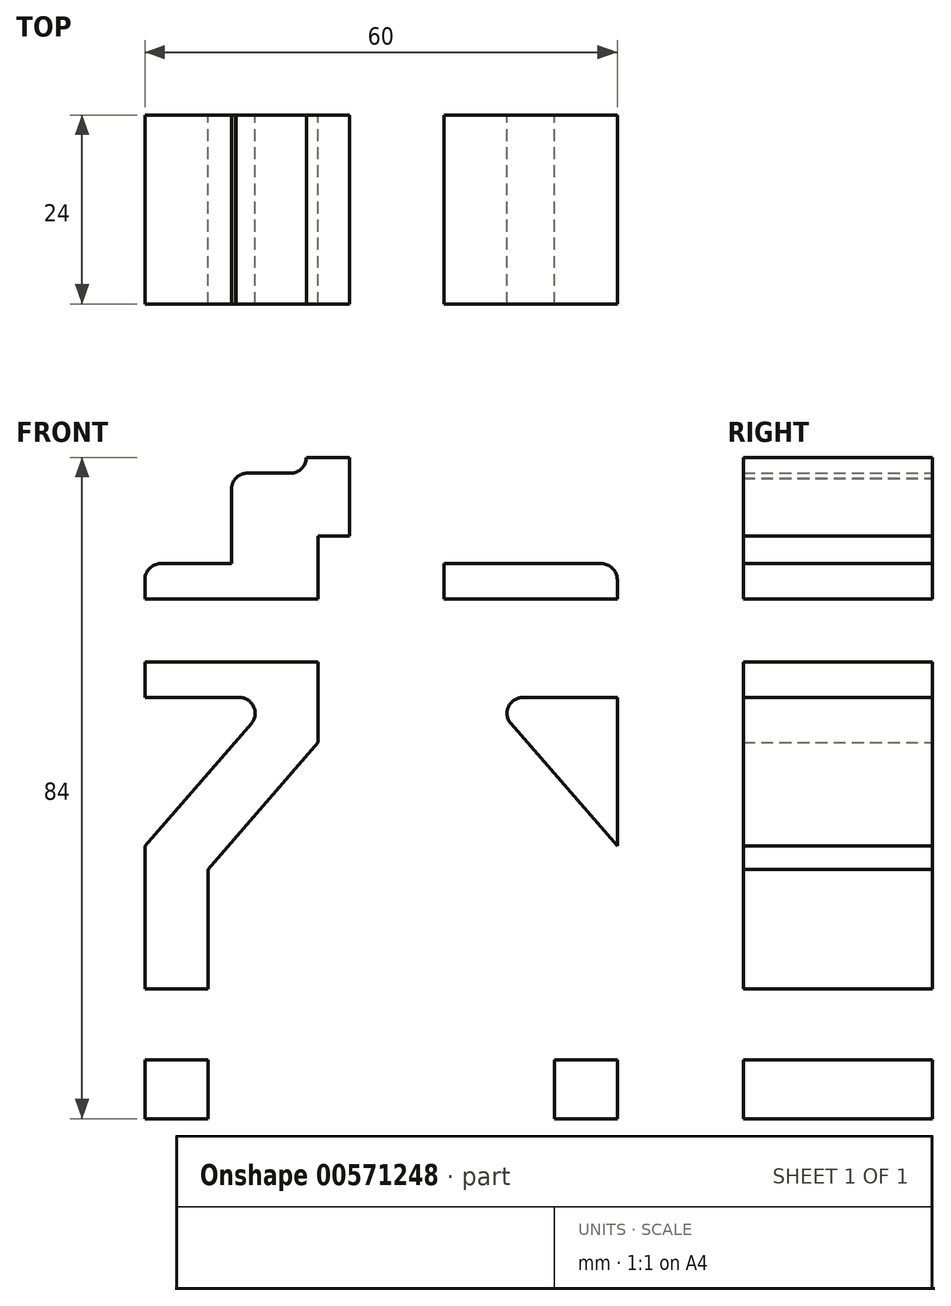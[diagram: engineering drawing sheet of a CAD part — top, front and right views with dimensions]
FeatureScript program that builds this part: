
annotation { "Feature Type Name" : "Feature", "Feature Type Description" : "" }
export const myFeature = defineFeature(function(context is Context, id is Id, definition is map)
    precondition{}
    {
        {
            var Q0;
            Q0=qCreatedBy(makeId("Front.planeOp"),FACE);
            var sketch = newSketch(context, id + "F0", { "sketchPlane" : qUnion([Q0])});
            skLineSegment(sketch, "E0", {"start": v(0, 0) * mm, "end": v(0, 72) * mm, "construction": true});
            skLineSegment(sketch, "E1", {"start": v(0, 72) * mm, "end": v(-4, 72) * mm});
            skLineSegment(sketch, "E2", {"start": v(-4, 72) * mm, "end": v(-4, 62) * mm});
            skLineSegment(sketch, "E3", {"start": v(0, 62) * mm, "end": v(-8, 62) * mm});
            skLineSegment(sketch, "E4", {"start": v(-8, 62) * mm, "end": v(-8, 35.76) * mm});
            skLineSegment(sketch, "E5", {"start": v(0, 50) * mm, "end": v(-30, 50) * mm, "construction": true});
            skLineSegment(sketch, "E6", {"start": v(-30, 54) * mm, "end": v(-8, 54) * mm});
            skLineSegment(sketch, "E7.MirrorCS", {"start": v(-30, 46) * mm, "end": v(-8, 46) * mm});
            skLineSegment(sketch, "E8", {"start": v(-22, 19.66) * mm, "end": v(-22, -12) * mm});
            skLineSegment(sketch, "E9", {"start": v(-22, -12) * mm, "end": v(-30, -12) * mm});
            skLineSegment(sketch, "E10", {"start": v(-30, 0) * mm, "end": v(0, 0) * mm, "construction": true});
            skLineSegment(sketch, "E11", {"start": v(-30, 41.5) * mm, "end": v(-18, 41.5) * mm});
            skLineSegment(sketch, "E12", {"start": v(-30, 22.65) * mm, "end": v(-16.5, 38.19) * mm});
            skLineSegment(sketch, "E13", {"start": v(-30, 22.65) * mm, "end": v(-30, 54) * mm});
            skLineSegment(sketch, "E14", {"start": v(-30, 54) * mm, "end": v(-30, 56.5) * mm});
            skLineSegment(sketch, "E15", {"start": v(-28, 58.5) * mm, "end": v(-8, 58.5) * mm});
            skArc(sketch, "E16.filletArc", {"start": v(-16.5, 38.19) * mm, "mid": v(-16.18, 40.33) * mm, "end": v(-18, 41.5) * mm});
            skLineSegment(sketch, "E17", {"start": v(-30, -12) * mm, "end": v(-30, 22.65) * mm});
            skLineSegment(sketch, "E18", {"start": v(-30, 4.5) * mm, "end": v(-22, 4.5) * mm});
            skLineSegment(sketch, "E19", {"start": v(-30, -4.5) * mm, "end": v(-22, -4.5) * mm});
            skLineSegment(sketch, "E20", {"start": v(-22, 19.66) * mm, "end": v(-8, 35.76) * mm});
            skLineSegment(sketch, "E21", {"start": v(-19, 58.5) * mm, "end": v(-19, 68) * mm});
            skLineSegment(sketch, "E22", {"start": v(-4, 72) * mm, "end": v(-9.5, 72) * mm});
            skLineSegment(sketch, "E23", {"start": v(-11.5, 70) * mm, "end": v(-17, 70) * mm});
            skPoint(sketch, "E24.visualSharp", {"position": v(-9.5, 70) * mm});
            skArc(sketch, "E24.filletArc", {"start": v(-11.5, 70) * mm, "mid": v(-10.09, 70.59) * mm, "end": v(-9.5, 72) * mm});
            skArc(sketch, "E25.filletArc", {"start": v(-17, 70) * mm, "mid": v(-18.41, 69.41) * mm, "end": v(-19, 68) * mm});
            skPoint(sketch, "E26.visualSharp", {"position": v(-30, 58.5) * mm});
            skArc(sketch, "E26.filletArc", {"start": v(-28, 58.5) * mm, "mid": v(-29.41, 57.91) * mm, "end": v(-30, 56.5) * mm});
            skLineSegment(sketch, "E27", {"start": v(-29.41, 57.91) * mm, "end": v(-18.41, 69.41) * mm});
            skLineSegment(sketch, "E28.MirrorCS", {"start": v(30, 54) * mm, "end": v(30, 56.5) * mm});
            skArc(sketch, "E29.MirrorCS", {"start": v(28, 58.5) * mm, "mid": v(29.41, 57.91) * mm, "end": v(30, 56.5) * mm});
            skArc(sketch, "E30.MirrorCS", {"start": v(17, 70) * mm, "mid": v(18.41, 69.41) * mm, "end": v(19, 68) * mm});
            skArc(sketch, "E31.MirrorCS", {"start": v(11.5, 70) * mm, "mid": v(10.09, 70.59) * mm, "end": v(9.5, 72) * mm});
            skArc(sketch, "E32.MirrorCS", {"start": v(16.5, 38.19) * mm, "mid": v(16.18, 40.33) * mm, "end": v(18, 41.5) * mm});
            skLineSegment(sketch, "E33.MirrorCS", {"start": v(30, 54) * mm, "end": v(8, 54) * mm});
            skLineSegment(sketch, "E34.MirrorCS", {"start": v(30, 41.5) * mm, "end": v(18, 41.5) * mm});
            skPoint(sketch, "E35.MirrorP", {"position": v(9.5, 70) * mm});
            skLineSegment(sketch, "E36.MirrorCS", {"start": v(28, 58.5) * mm, "end": v(8, 58.5) * mm});
            skLineSegment(sketch, "E37.MirrorCS", {"start": v(30, 22.65) * mm, "end": v(16.5, 38.19) * mm});
            skLineSegment(sketch, "E38.MirrorCS", {"start": v(29.41, 57.91) * mm, "end": v(18.41, 69.41) * mm});
            skLineSegment(sketch, "E39.MirrorCS", {"start": v(11.5, 70) * mm, "end": v(17, 70) * mm});
            skLineSegment(sketch, "E40.MirrorCS", {"start": v(22, 19.66) * mm, "end": v(8, 35.76) * mm});
            skLineSegment(sketch, "E41.MirrorCS", {"start": v(30, 22.65) * mm, "end": v(30, 54) * mm});
            skLineSegment(sketch, "E42.MirrorCS", {"start": v(30, -12) * mm, "end": v(30, 22.65) * mm});
            skLineSegment(sketch, "E43.MirrorCS", {"start": v(0, 50) * mm, "end": v(30, 50) * mm, "construction": true});
            skLineSegment(sketch, "E44.MirrorCS", {"start": v(30, 0) * mm, "end": v(0, 0) * mm, "construction": true});
            skLineSegment(sketch, "E45.MirrorCS", {"start": v(8, 62) * mm, "end": v(8, 35.76) * mm});
            skLineSegment(sketch, "E46.MirrorCS", {"start": v(0, 72) * mm, "end": v(4, 72) * mm});
            skLineSegment(sketch, "E47.MirrorCS", {"start": v(22, 19.66) * mm, "end": v(22, -12) * mm});
            skLineSegment(sketch, "E48.MirrorCS", {"start": v(4, 72) * mm, "end": v(9.5, 72) * mm});
            skLineSegment(sketch, "E49.MirrorCS", {"start": v(22, -12) * mm, "end": v(30, -12) * mm});
            skLineSegment(sketch, "E50.MirrorCS", {"start": v(19, 58.5) * mm, "end": v(19, 68) * mm});
            skLineSegment(sketch, "E51.MirrorCS", {"start": v(0, 62) * mm, "end": v(8, 62) * mm});
            skLineSegment(sketch, "E52.MirrorCS", {"start": v(4, 72) * mm, "end": v(4, 62) * mm});
            skLineSegment(sketch, "E53.MirrorCS", {"start": v(30, -4.5) * mm, "end": v(22, -4.5) * mm});
            skLineSegment(sketch, "E54.MirrorCS", {"start": v(30, 46) * mm, "end": v(8, 46) * mm});
            skLineSegment(sketch, "E55.MirrorCS", {"start": v(30, 4.5) * mm, "end": v(22, 4.5) * mm});
            skPoint(sketch, "E56.MirrorP", {"position": v(30, 58.5) * mm});
            skSolve(sketch);
        }
        {
            var Q0;
            {var subQ6=sQuery(id+"F0.wireOp",EDGE,"E2");Q0=makeQuery(id+"F0.imprint","IMPRINT",FACE,{"disambiguationData":[TD([[makeQuery(id+"F0.imprint","IMPRINT",EDGE,{"derivedFrom":subQ6}),-1.0]])]});}
            var Q1;
            {var subQ1=sQuery(id+"F0.wireOp",EDGE,"E6");Q1=makeQuery(id+"F0.imprint","IMPRINT",FACE,{"disambiguationData":[TD([[makeQuery(id+"F0.imprint","IMPRINT",EDGE,{"derivedFrom":subQ1}),1.0]])]});}
            var Q2;
            {var subQ7=sQuery(id+"F0.wireOp",EDGE,"E7.MirrorCS");Q2=makeQuery(id+"F0.imprint","IMPRINT",FACE,{"disambiguationData":[TD([[makeQuery(id+"F0.imprint","IMPRINT",EDGE,{"derivedFrom":subQ7}),-1.0]])]});}
            var Q3;
            {var subQ0=sQuery(id+"F0.wireOp",EDGE,"E9");Q3=makeQuery(id+"F0.imprint","IMPRINT",FACE,{"disambiguationData":[TD([[makeQuery(id+"F0.imprint","IMPRINT",EDGE,{"derivedFrom":subQ0}),-1.0]])]});}
            var Q4;
            {var subQ0=sQuery(id+"F0.wireOp",EDGE,"E49.MirrorCS");Q4=makeQuery(id+"F0.imprint","IMPRINT",FACE,{"disambiguationData":[TD([[makeQuery(id+"F0.imprint","IMPRINT",EDGE,{"derivedFrom":subQ0}),1.0]])]});}
            var Q5;
            Q5=makeQuery(id+"F0.imprint","IMPRINT",FACE,{"disambiguationData":[TD([[makeQuery(id+"F0.imprint","IMPRINT",EDGE,{"derivedFrom":sQuery(id+"F0.wireOp",EDGE,"E32.MirrorCS")}),1.0]])]});
            var Q6;
            {var subQ4=sQuery(id+"F0.wireOp",EDGE,"E28.MirrorCS");Q6=makeQuery(id+"F0.imprint","IMPRINT",FACE,{"disambiguationData":[TD([[makeQuery(id+"F0.imprint","IMPRINT",EDGE,{"derivedFrom":subQ4}),1.0]])]});}
            var Q7;
            Q7=makeQuery(id+"F0.imprint","IMPRINT",FACE,{"disambiguationData":[TD([[makeQuery(id+"F0.imprint","IMPRINT",EDGE,{"derivedFrom":sQuery(id+"F0.wireOp",EDGE,"E31.MirrorCS")}),1.0]])]});
            extrude(context, id + "F1", {"entities" : qUnion([Q0, Q1, Q2, Q3, Q4, Q5, Q6, Q7]), "depth" : 24 * mm, "offsetDistance" : 25 * mm});
        }
    });
